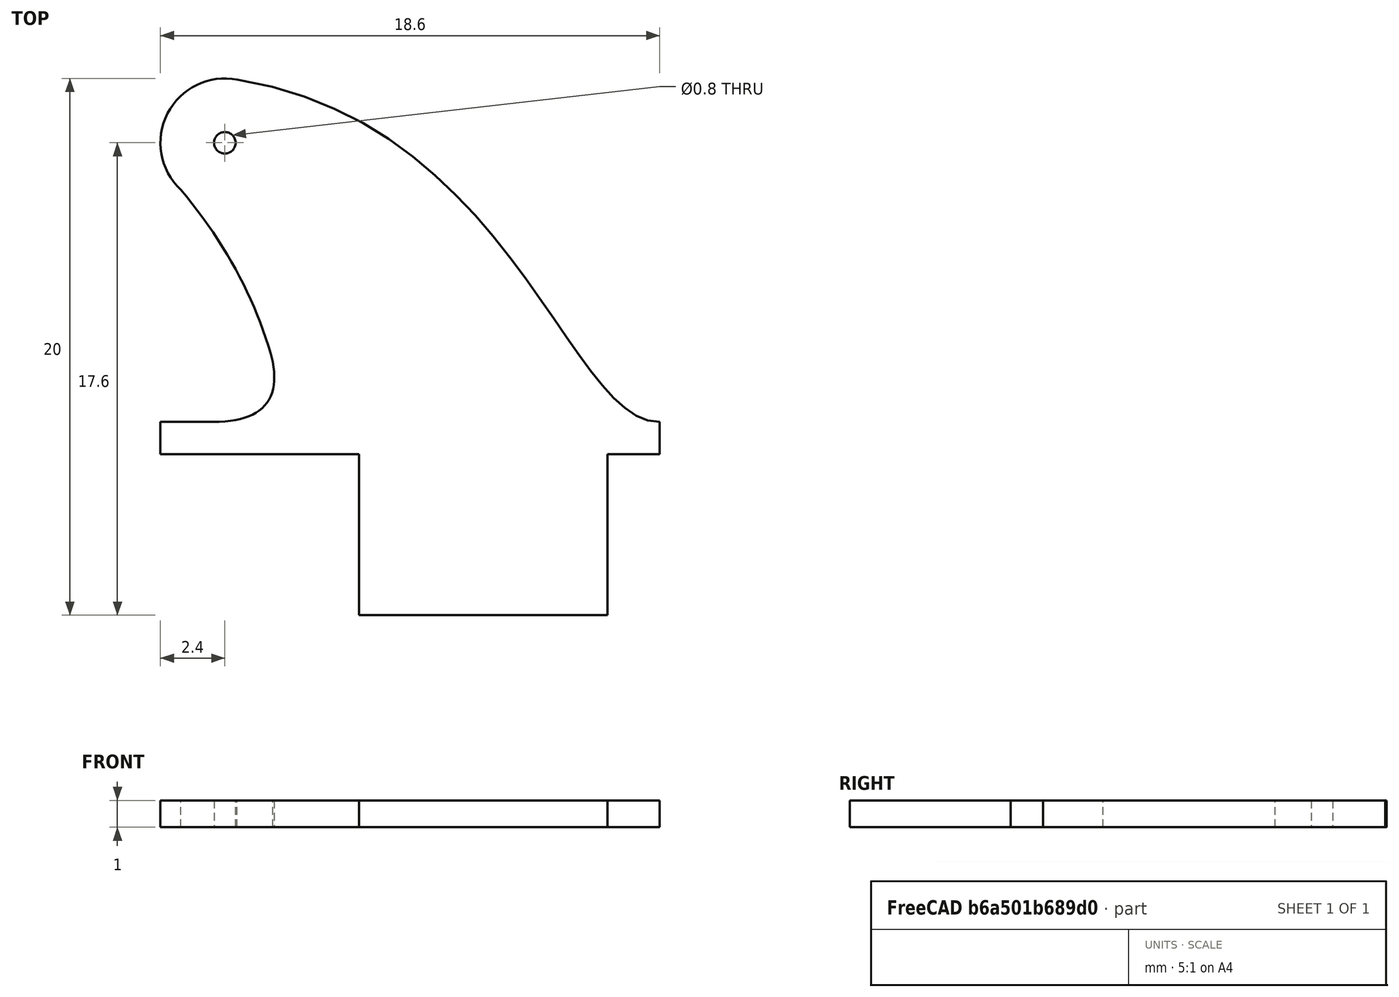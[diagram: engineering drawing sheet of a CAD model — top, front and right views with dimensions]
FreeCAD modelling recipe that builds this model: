
FCSTD DOCUMENT  (FreeCAD 0.20R0.20.2)
Label: 005
License: All rights reserved
LicenseURL: http://en.wikipedia.org/wiki/All_rights_reserved
objects: Sketcher::SketchObject×2, Part::Extrusion×1
note: 3 computed .brp shape members not serialized (recipe doc carries the construction recipe); baked Part::Feature solids carry a one-line shape summary decoded from their .brp

FEATURE [Sketcher::SketchObject] Sketch  label="main"
  FullyConstrained = true
  sketch-geometry (25):
    g0: LineSegment StartX=12.0586 StartY=-6 StartZ=0 EndX=12.0586 EndY=0 EndZ=0
    g1: LineSegment StartX=2.8 StartY=-6 StartZ=0 EndX=2.8 EndY=0 EndZ=0
    g2: LineSegment StartX=2.8 StartY=-6 StartZ=0 EndX=12.0586 EndY=-6 EndZ=0
    g3: LineSegment StartX=12.0586 StartY=0 StartZ=0 EndX=14 EndY=0 EndZ=0
    g4: LineSegment StartX=2.8 StartY=0 StartZ=0 EndX=0 EndY=0 EndZ=0
    g5: LineSegment StartX=14 StartY=0 StartZ=0 EndX=14 EndY=1.2 EndZ=0
    g6: LineSegment StartX=0 StartY=0 StartZ=0 EndX=-4.6 EndY=0 EndZ=0
    g7: Circle CenterX=-2.2 CenterY=11.6 CenterZ=0 NormalX=0 NormalY=0 NormalZ=1 AngleXU=0 Radius=0.4
    g8-g11: Circle x4 (B-spline internal-alignment scaffolding for g12; pole/knot coordinates omitted)
    g12: BSplineCurve PolesCount=4 KnotsCount=2 Degree=3 IsPeriodic=0
    g13: GeomPoint X=-1.74436 Y=13.9564 Z=0
    g14: GeomPoint X=14 Y=1.2 Z=0
    g15: ArcOfCircle CenterX=-2.2 CenterY=11.6 CenterZ=0 NormalX=0 NormalY=0 NormalZ=1 AngleXU=0 Radius=2.4 StartAngle=1.37979 EndAngle=3.95565
    g16: LineSegment StartX=-2.62672 StartY=1.2 StartZ=0 EndX=-4.6 EndY=1.2 EndZ=0
    g17: LineSegment StartX=-4.6 StartY=0 StartZ=0 EndX=-4.6 EndY=1.2 EndZ=0
    g18: Circle CenterX=-2.62672 CenterY=1.2 CenterZ=0 NormalX=0 NormalY=0 NormalZ=1 AngleXU=0 Radius=1
    g19: Circle CenterX=0 CenterY=1.2 CenterZ=0 NormalX=0 NormalY=0 NormalZ=1 AngleXU=0 Radius=1
    g20: Circle CenterX=-0.413885 CenterY=3.44541 CenterZ=0 NormalX=0 NormalY=0 NormalZ=1 AngleXU=0 Radius=1
    g21: BSplineCurve PolesCount=3 KnotsCount=2 Degree=2 IsPeriodic=0
    g22: GeomPoint X=-2.62672 Y=1.2 Z=0
    g23: GeomPoint X=-0.413885 Y=3.44541 Z=0
    g24: BSplineCurve PolesCount=3 KnotsCount=2 Degree=2 IsPeriodic=0
  constraints (52):
    c: Vertical(g0)
    c: Vertical(g1)
    c: Block(g1)
    c: Block(g0)
    c: Distance(g1) = 6
    c: Coincident(g2,g1)
    c: Horizontal(g2)
    c: Coincident(g0,g2)
    c: Block(g2)
    c: Coincident(g3,g0)
    c: Horizontal(g3)
    c: Coincident(g4,g1)
    c: Horizontal(g4)
    c: Block(g3)
    c: Block(g4)
    c: Coincident(g5,g3)
    c: Vertical(g5)
    c: Distance(g5) = 1.2
    c: Coincident(g6,g4)
    c: Horizontal(g6)
    c: Distance(g6) = 4.6
    c: Block(g7)
    c: Weight(g8) = 1
    c: Equal(g8,g9)
    c: Equal(g8,g10)
    c: Equal(g8,g11)
    c: Coincident(g12,g5)
    c: InternalAlignment(g8-g11 -> g12) x4
    c: InternalAlignment(g13,g12)
    c: InternalAlignment(g14,g12)
    c: Block(g12)
    c: Coincident(g15,g7)
    c: Coincident(g15,g12)
    c: Coincident(g15,g24)
    c: Block(g15)
    c: Horizontal(g16)
    c: Coincident(g17,g6)
    c: Vertical(g17)
    c: Coincident(g17,g16)
    c: Weight(g18) = 1
    c: Equal(g18,g19)
    c: Equal(g18,g20)
    c: InternalAlignment(g18,g21)
    c: InternalAlignment(g19,g21)
    c: InternalAlignment(g20,g21)
    c: InternalAlignment(g22,g21)
    c: InternalAlignment(g23,g21)
    c: Block(g16)
    c: Coincident(g16,g21)
    c: Coincident(g21,g24)
    c: Block(g24)
    c: Block(g21)
FEATURE [Part::Extrusion] Extrude
  Base = -> Sketch
  Dir = (0,0,1)
  DirMode = 2
  FaceMakerClass = Part::FaceMakerBullseye
  LengthFwd = 1
  LengthRev = 0
  Solid = true
  Symmetric = false
FEATURE [Sketcher::SketchObject] Sketch001  label="main001"
  FullyConstrained = true
  sketch-geometry (42):
    g0: LineSegment StartX=12.0586 StartY=-6 StartZ=0 EndX=12.0586 EndY=0 EndZ=0
    g1: LineSegment StartX=2.8 StartY=-6 StartZ=0 EndX=2.8 EndY=0 EndZ=0
    g2: LineSegment StartX=2.8 StartY=-6 StartZ=0 EndX=12.0586 EndY=-6 EndZ=0
    g3: LineSegment StartX=12.0586 StartY=0 StartZ=0 EndX=14 EndY=0 EndZ=0
    g4: LineSegment StartX=2.8 StartY=0 StartZ=0 EndX=0 EndY=0 EndZ=0
    g5: LineSegment StartX=14 StartY=0 StartZ=0 EndX=14 EndY=1.2 EndZ=0
    g6: LineSegment StartX=0 StartY=0 StartZ=0 EndX=-4.6 EndY=0 EndZ=0
    g7: Circle CenterX=-2.2 CenterY=11.6 CenterZ=0 NormalX=0 NormalY=0 NormalZ=1 AngleXU=0 Radius=0.4
    g8-g11: Circle x4 (B-spline internal-alignment scaffolding for g12; pole/knot coordinates omitted)
    g12: BSplineCurve PolesCount=4 KnotsCount=2 Degree=3 IsPeriodic=0
    g13: GeomPoint X=-1.74436 Y=13.9564 Z=0
    g14: GeomPoint X=14 Y=1.2 Z=0
    g15: ArcOfCircle CenterX=-2.2 CenterY=11.6 CenterZ=0 NormalX=0 NormalY=0 NormalZ=1 AngleXU=0 Radius=2.4 StartAngle=1.37979 EndAngle=3.95565
    g16: LineSegment StartX=-2.62672 StartY=1.2 StartZ=0 EndX=-4.6 EndY=1.2 EndZ=0
    g17: LineSegment StartX=-4.6 StartY=0 StartZ=0 EndX=-4.6 EndY=1.2 EndZ=0
    g18: Circle CenterX=-2.62672 CenterY=1.2 CenterZ=0 NormalX=0 NormalY=0 NormalZ=1 AngleXU=0 Radius=1
    g19: Circle CenterX=0 CenterY=1.2 CenterZ=0 NormalX=0 NormalY=0 NormalZ=1 AngleXU=0 Radius=1
    g20: Circle CenterX=-0.413885 CenterY=3.44541 CenterZ=0 NormalX=0 NormalY=0 NormalZ=1 AngleXU=0 Radius=1
    g21: BSplineCurve PolesCount=3 KnotsCount=2 Degree=2 IsPeriodic=0
    g22: GeomPoint X=-2.62672 Y=1.2 Z=0
    g23: GeomPoint X=-0.413885 Y=3.44541 Z=0
    g24: BSplineCurve PolesCount=3 KnotsCount=2 Degree=2 IsPeriodic=0
    g25: LineSegment StartX=-2.2 StartY=11.6 StartZ=0 EndX=-0.6 EndY=11.6 EndZ=0
    g26: Circle CenterX=-2.2 CenterY=11.6 CenterZ=0 NormalX=0 NormalY=0 NormalZ=1 AngleXU=0 Radius=1.6
    g27: LineSegment StartX=0 StartY=1.2 StartZ=0 EndX=1.34801 EndY=2.51783 EndZ=0
    g28: LineSegment StartX=-0.413885 StartY=3.44541 StartZ=0 EndX=-0.249951 EndY=7.1888 EndZ=0
    g29: Circle CenterX=-3.3091 CenterY=10.4468 CenterZ=0 NormalX=0 NormalY=0 NormalZ=1 AngleXU=0 Radius=1
    g30: Circle CenterX=-0.249951 CenterY=7.1888 CenterZ=0 NormalX=0 NormalY=0 NormalZ=1 AngleXU=0 Radius=1
    g31: Circle CenterX=1.34801 CenterY=2.51783 CenterZ=0 NormalX=0 NormalY=0 NormalZ=1 AngleXU=0 Radius=1
    g32: BSplineCurve PolesCount=3 KnotsCount=2 Degree=2 IsPeriodic=0
    g33: GeomPoint X=-3.3091 Y=10.4468 Z=0
    g34: GeomPoint X=1.34801 Y=2.51783 Z=0
    g35: LineSegment StartX=0 StartY=1.2 StartZ=0 EndX=3.28198 EndY=1.2 EndZ=0
    g36: Circle CenterX=1.34801 CenterY=2.51783 CenterZ=0 NormalX=0 NormalY=0 NormalZ=1 AngleXU=0 Radius=1
    g37: Circle CenterX=1.8831 CenterY=1.2 CenterZ=0 NormalX=0 NormalY=0 NormalZ=1 AngleXU=0 Radius=1
    g38: Circle CenterX=3.28198 CenterY=1.2 CenterZ=0 NormalX=0 NormalY=0 NormalZ=1 AngleXU=0 Radius=1
    g39: BSplineCurve PolesCount=3 KnotsCount=2 Degree=2 IsPeriodic=0
    g40: GeomPoint X=1.34801 Y=2.51783 Z=0
    g41: GeomPoint X=3.28198 Y=1.2 Z=0
  constraints (84):
    c: Vertical(g0)
    c: Vertical(g1)
    c: Block(g1)
    c: Block(g0)
    c: Distance(g1) = 6
    c: Coincident(g2,g1)
    c: Horizontal(g2)
    c: Coincident(g0,g2)
    c: Block(g2)
    c: Coincident(g3,g0)
    c: Horizontal(g3)
    c: Coincident(g4,g1)
    c: Horizontal(g4)
    c: Block(g3)
    c: Block(g4)
    c: Coincident(g5,g3)
    c: Vertical(g5)
    c: Distance(g5) = 1.2
    c: Coincident(g6,g4)
    c: Horizontal(g6)
    c: Distance(g6) = 4.6
    c: Block(g7)
    c: Weight(g8) = 1
    c: Equal(g8,g9)
    c: Equal(g8,g10)
    c: Equal(g8,g11)
    c: Coincident(g12,g5)
    c: InternalAlignment(g8-g11 -> g12) x4
    c: InternalAlignment(g13,g12)
    c: InternalAlignment(g14,g12)
    c: Block(g12)
    c: Coincident(g15,g7)
    c: Coincident(g15,g12)
    c: Coincident(g15,g24)
    c: Block(g15)
    c: Horizontal(g16)
    c: Coincident(g17,g6)
    c: Vertical(g17)
    c: Coincident(g17,g16)
    c: Weight(g18) = 1
    c: Equal(g18,g20)
    c: InternalAlignment(g18,g21)
    c: InternalAlignment(g19,g21)
    c: InternalAlignment(g20,g21)
    c: InternalAlignment(g22,g21)
    c: InternalAlignment(g23,g21)
    c: Block(g16)
    c: Coincident(g16,g21)
    c: Coincident(g21,g24)
    c: Block(g24)
    c: Block(g21)
    c: Coincident(g25,g7)
    c: Horizontal(g25)
    c: Distance(g25) = 1.6
    c: Coincident(g26,g7)
    c: PointOnObject(g25,g26)
    c: Coincident(g27,g19)
    c: Coincident(g28,g21)
    c: Weight(g29) = 1
    c: PointOnObject(g32,g26)
    c: Equal(g29,g30)
    c: Coincident(g30,g28)
    c: Equal(g29,g31)
    c: Coincident(g32,g27)
    c: InternalAlignment(g29,g32)
    c: InternalAlignment(g30,g32)
    c: InternalAlignment(g31,g32)
    c: InternalAlignment(g33,g32)
    c: InternalAlignment(g34,g32)
    c: Block(g32)
    c: Coincident(g35,g27)
    c: Horizontal(g35)
    c: Weight(g36) = 1
    c: Coincident(g39,g27)
    c: Equal(g36,g37)
    c: PointOnObject(g37,g35)
    c: Equal(g36,g38)
    c: Coincident(g39,g35)
    c: InternalAlignment(g36,g39)
    c: InternalAlignment(g37,g39)
    c: InternalAlignment(g38,g39)
    c: InternalAlignment(g40,g39)
    c: InternalAlignment(g41,g39)
    c: Block(g39)
